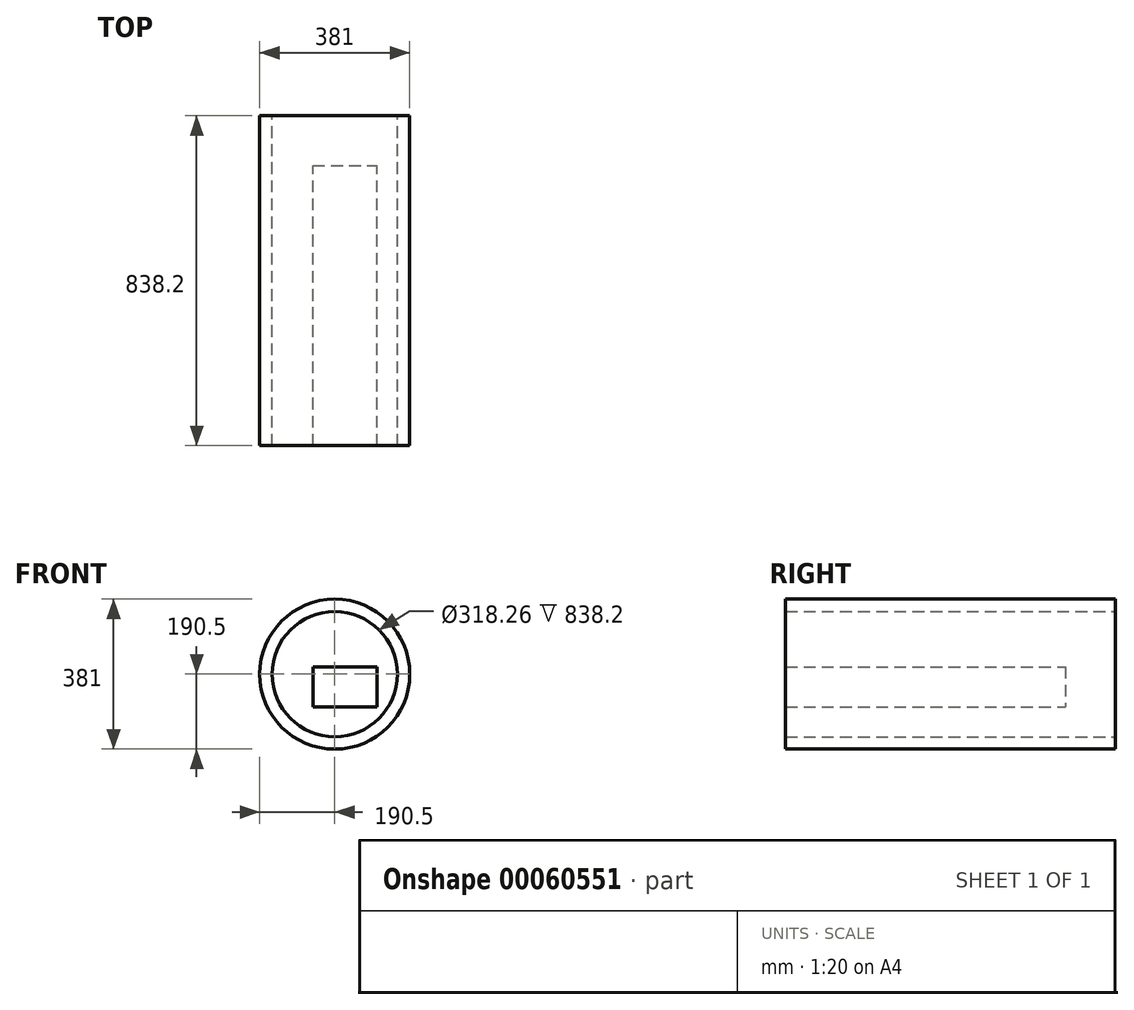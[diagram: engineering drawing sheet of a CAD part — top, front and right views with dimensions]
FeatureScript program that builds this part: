
annotation { "Feature Type Name" : "Feature", "Feature Type Description" : "" }
export const myFeature = defineFeature(function(context is Context, id is Id, definition is map)
    precondition{}
    {
        {
            var Q0;
            Q0=qCreatedBy(makeId("Front.planeOp"),FACE);
            var sketch = newSketch(context, id + "F0", { "sketchPlane" : qUnion([Q0])});
            skCircle(sketch, "E0", {"center": v(0, 0) * mm, "radius": 190.5 * mm});
            skCircle(sketch, "E1", {"center": v(0, 0) * mm, "radius": 159.13 * mm});
            skSolve(sketch);
        }
        {
            var Q0;
            Q0 = qSketchRegion(id + "F0", true);
            extrude(context, id + "F1", {"entities" : qUnion([Q0]), "depth" : 711.2 * mm, "hasSecondDirection" : true, "secondDirectionOppositeDirection" : true, "secondDirectionDepth" : 127 * mm});
        }
        {
            var Q0;
            Q0=qCreatedBy(makeId("Front.planeOp"),FACE);
            var sketch = newSketch(context, id + "F2", { "sketchPlane" : qUnion([Q0])});
            skLineSegment(sketch, "E2.bottom", {"start": v(-55.4, 18.8) * mm, "end": v(107.36, 18.8) * mm});
            skLineSegment(sketch, "E2.top", {"start": v(-55.4, -83.77) * mm, "end": v(107.36, -83.77) * mm});
            skLineSegment(sketch, "E2.left", {"start": v(-55.4, 18.8) * mm, "end": v(-55.4, -83.77) * mm});
            skLineSegment(sketch, "E2.right", {"start": v(107.36, 18.8) * mm, "end": v(107.36, -83.77) * mm});
            skSolve(sketch);
        }
        {
            var Q0;
            Q0 = qSketchRegion(id + "F2", true);
            extrude(context, id + "F3", {"entities" : qUnion([Q0]), "depth" : 711.2 * mm});
        }
    });
